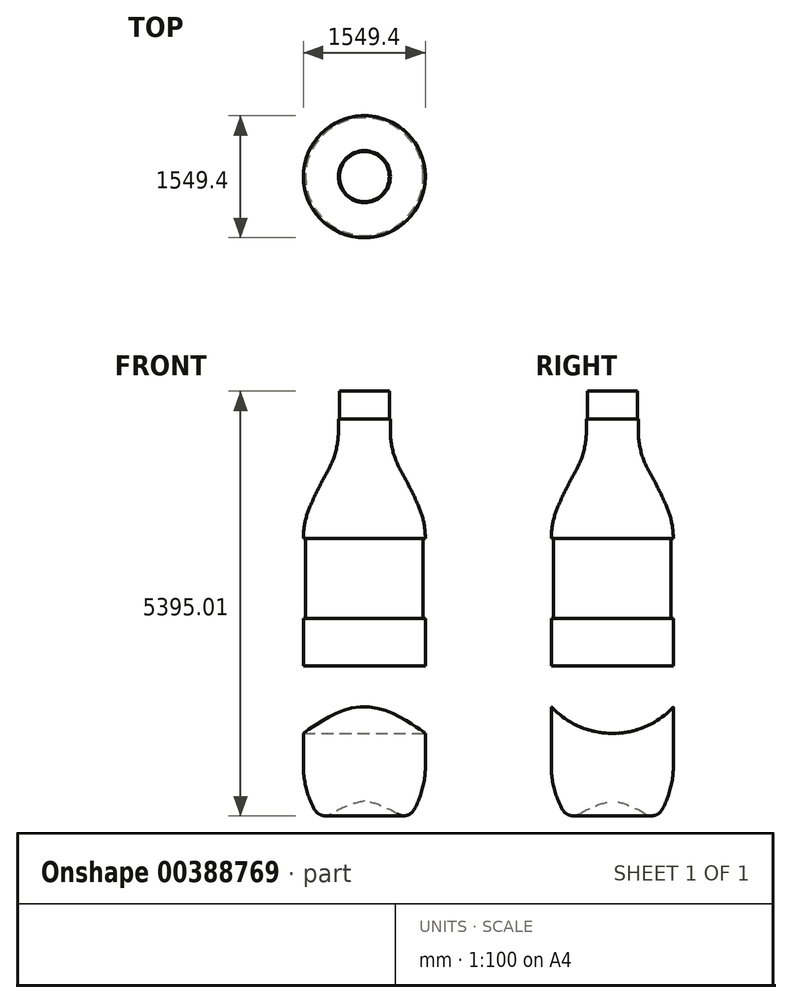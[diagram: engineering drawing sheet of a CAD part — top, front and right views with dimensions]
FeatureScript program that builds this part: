
annotation { "Feature Type Name" : "Feature", "Feature Type Description" : "" }
export const myFeature = defineFeature(function(context is Context, id is Id, definition is map)
    precondition{}
    {
        {
            var Q0;
            Q0=qCreatedBy(makeId("Front.planeOp"),FACE);
            var sketch = newSketch(context, id + "F0", { "sketchPlane" : qUnion([Q0])});
            skLineSegment(sketch, "E0.bottom", {"start": v(0, 0) * mm, "end": v(-774.7, 0) * mm, "construction": true});
            skLineSegment(sketch, "E0.top", {"start": v(0, 5397.5) * mm, "end": v(-774.7, 5397.5) * mm, "construction": true});
            skLineSegment(sketch, "E0.left", {"start": v(0, 0) * mm, "end": v(0, 5397.5) * mm, "construction": true});
            skLineSegment(sketch, "E0.right", {"start": v(-774.7, 0) * mm, "end": v(-774.7, 5397.5) * mm, "construction": true});
            skLineSegment(sketch, "E1", {"start": v(0, 5397.5) * mm, "end": v(-317.5, 5397.5) * mm});
            skLineSegment(sketch, "E2", {"start": v(-317.5, 5397.5) * mm, "end": v(-317.5, 5041.9) * mm});
            skLineSegment(sketch, "E3", {"start": v(-317.5, 5041.9) * mm, "end": v(-330.2, 5041.9) * mm});
            skLineSegment(sketch, "E4", {"start": v(-330.2, 5041.9) * mm, "end": v(-330.2, 4889.5) * mm});
            skArc(sketch, "E5", {"start": v(-330.2, 4889.5) * mm, "mid": v(-363.63, 4631.02) * mm, "end": v(-461.72, 4389.55) * mm});
            skArc(sketch, "E6", {"start": v(-461.72, 4389.55) * mm, "mid": v(-580.77, 4166.1) * mm, "end": v(-688.55, 3937) * mm});
            skArc(sketch, "E7", {"start": v(-688.55, 3937) * mm, "mid": v(-752.93, 3736.76) * mm, "end": v(-774.7, 3527.56) * mm});
            skLineSegment(sketch, "E8", {"start": v(-774.7, 3527.56) * mm, "end": v(-746.76, 3527.56) * mm});
            skLineSegment(sketch, "E9", {"start": v(-746.76, 3527.56) * mm, "end": v(-746.76, 2511.56) * mm});
            skLineSegment(sketch, "E10", {"start": v(-746.76, 2511.56) * mm, "end": v(-774.7, 2511.56) * mm});
            skLineSegment(sketch, "E11", {"start": v(-774.7, 2511.56) * mm, "end": v(-774.7, 635) * mm});
            skArc(sketch, "E12", {"start": v(-774.7, 635) * mm, "mid": v(-738.32, 348.9) * mm, "end": v(-631.48, 81.02) * mm});
            skArc(sketch, "E13", {"start": v(-631.48, 81.02) * mm, "mid": v(-535.8, 7.2) * mm, "end": v(-416.48, 26.24) * mm});
            skArc(sketch, "E14", {"start": v(-416.48, 26.24) * mm, "mid": v(-216.07, 128.22) * mm, "end": v(0, 190.5) * mm});
            skLineSegment(sketch, "E15", {"start": v(0, 5397.5) * mm, "end": v(0, 190.5) * mm});
            skSolve(sketch);
        }
        {
            var Q0;
            Q0=makeQuery(id+"F0.imprint","IMPRINT",FACE,{"disambiguationData":[TD([[makeQuery(id+"F0.imprint","IMPRINT",EDGE,{"derivedFrom":sQuery(id+"F0.wireOp",EDGE,"E1")}),1.0]])]});
            var Q1;
            Q1=sQuery(id+"F0.wireOp",EDGE,"E15");
            revolve(context, id + "F1", {"entities" : qUnion([Q0]), "axis" : qUnion([Q1]), "revolveType" : RevolveType.FULL});
        }
        {
            var Q0;
            Q0=qCreatedBy(makeId("Right.planeOp"),FACE);
            var sketch = newSketch(context, id + "F2", { "sketchPlane" : qUnion([Q0])});
            skLineSegment(sketch, "E16", {"start": v(774.7, 2511.56) * mm, "end": v(774.7, 635) * mm});
            skLineSegment(sketch, "E17", {"start": v(-774.7, 635) * mm, "end": v(-774.7, 2511.56) * mm});
            skLineSegment(sketch, "E18", {"start": v(-774.7, 1905.73) * mm, "end": v(774.7, 1905.73) * mm});
            skArc(sketch, "E19", {"start": v(-774.7, 1388.6) * mm, "mid": v(-1.34, 1049.51) * mm, "end": v(774.7, 1382.43) * mm});
            skSolve(sketch);
        }
        {
            var Q0;
            Q0 = qSketchRegion(id + "F2", true);
            extrude(context, id + "F3", {"entities" : qUnion([Q0]), "operationType" : NewBodyOperationType.REMOVE, "endBound" : BoundingType.SYMMETRIC, "oppositeDirection" : true, "depth" : 2032 * mm});
        }
        {
            var Q0;
            Q0=qCreatedBy(makeId("Front.planeOp"),FACE);
            var Q1;
            Q1=qCreatedBy(makeId("Right.planeOp"),FACE);
            cPlane(context, id + "F4", {"entities" : qUnion([Q0, Q1]), "cplaneType" : CPlaneType.MID_PLANE, "offset" : 25.4 * mm, "width" : 152.4 * mm, "height" : 152.4 * mm});
        }
    });
